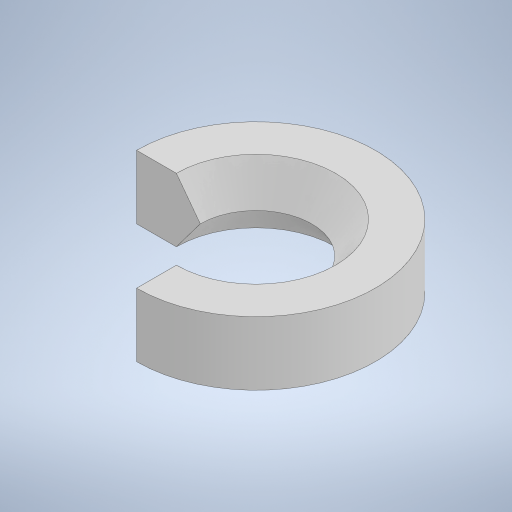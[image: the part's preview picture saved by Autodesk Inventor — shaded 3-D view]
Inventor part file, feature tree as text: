
AUTODESK INVENTOR PART (.ipt)
format: ipt  version: 2024 (Build 280153000, 153)  size: 257,536 bytes
history: native  units: mm
features: sketch x2, extrude x1, revolve x1
ambient origin geometry x8: Origin, YZ Plane, XZ Plane, XY Plane, X Axis, Y Axis, Z Axis, Center Point
bodies: Volumenkörper1 (feature_tree)
feature tree (4):
  extrude  "Extrusion1"  Depth=10.0mm
  revolve  "Umdrehung1"
  sketch  "Skizze1"  dims[d0=10.0mm d1=15.0mm]
  sketch  "Skizze2"  dims[d2=4.0mm d3=0.0mm d4=1.5mm d5=270.0deg]
